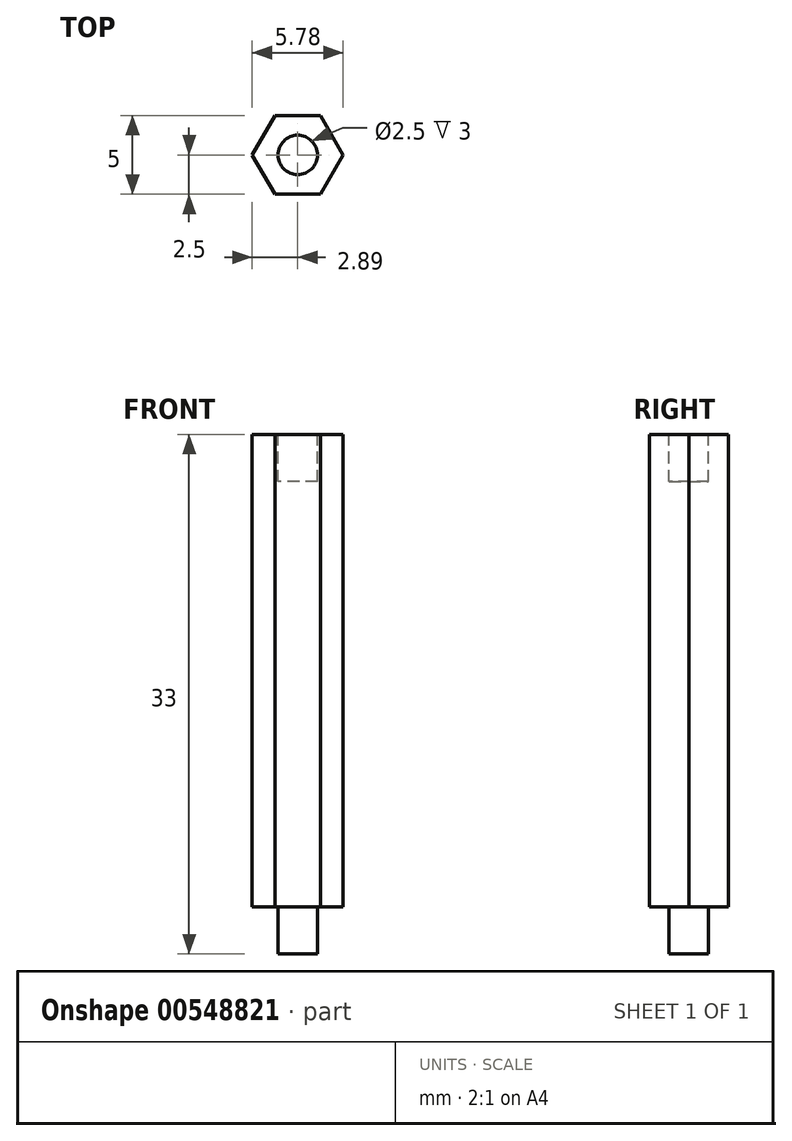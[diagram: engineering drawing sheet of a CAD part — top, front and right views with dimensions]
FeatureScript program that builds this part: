
annotation { "Feature Type Name" : "Feature", "Feature Type Description" : "" }
export const myFeature = defineFeature(function(context is Context, id is Id, definition is map)
    precondition{}
    {
        {
            var Q0;
            Q0=qCreatedBy(makeId("Top.planeOp"),FACE);
            var sketch = newSketch(context, id + "F0", { "sketchPlane" : qUnion([Q0])});
            skCircle(sketch, "E0", {"center": v(0, 0) * mm, "radius": 1.25 * mm});
            skSolve(sketch);
        }
        {
            var Q0;
            Q0 = qSketchRegion(id + "F0", true);
            extrude(context, id + "F1", {"entities" : qUnion([Q0]), "endBound" : BoundingType.SYMMETRIC, "oppositeDirection" : true, "depth" : 3 * mm, "offsetDistance" : 25 * mm});
        }
        {
            var Q0;
            Q0=makeQuery(id+"F1.opExtrude","CAP_FACE",FACE,{"disambiguationData":[OSD([sQuery(id+"F0.wireOp",EDGE,"E0")])],"isStart":true});
            var sketch = newSketch(context, id + "F2", { "sketchPlane" : qUnion([Q0])});
            skCircle(sketch, "E1.cCircle", {"center": v(0, 0) * mm, "radius": 2.5 * mm, "construction": true});
            skLineSegment(sketch, "E1.0", {"start": v(1.44, -2.5) * mm, "end": v(-1.44, -2.5) * mm});
            skLineSegment(sketch, "E1.1", {"start": v(-1.44, -2.5) * mm, "end": v(-2.89, 0) * mm});
            skLineSegment(sketch, "E1.2", {"start": v(-2.89, 0) * mm, "end": v(-1.44, 2.5) * mm});
            skLineSegment(sketch, "E1.3", {"start": v(-1.44, 2.5) * mm, "end": v(1.44, 2.5) * mm});
            skLineSegment(sketch, "E1.4", {"start": v(1.44, 2.5) * mm, "end": v(2.89, 0) * mm});
            skLineSegment(sketch, "E1.5", {"start": v(2.89, 0) * mm, "end": v(1.44, -2.5) * mm});
            skPoint(sketch, "E1.0.midPoint", {"position": v(0, -2.5) * mm});
            skSolve(sketch);
        }
        {
            var Q0;
            Q0=makeQuery(id+"F2.imprint","IMPRINT",FACE,{"disambiguationData":[TD([[makeQuery(id+"F2.imprint","IMPRINT",EDGE,{"derivedFrom":sQuery(id+"F2.wireOp",EDGE,"E1.0")}),-1.0]])]});
            var Q1;
            Q1=makeQuery(id+"F2.imprint","IMPRINT",FACE,{"disambiguationData":[TD([[makeQuery(id+"F2.imprint","IMPRINT",EDGE,{"derivedFrom":makeQuery(id+"F1.opExtrude","CAP_EDGE",EDGE,{"disambiguationData":[OSD([sQuery(id+"F0.wireOp",EDGE,"E0")])],"isStart":true})}),1.0]])]});
            extrude(context, id + "F3", {"entities" : qUnion([Q0, Q1]), "operationType" : NewBodyOperationType.ADD, "depth" : 30 * mm, "offsetDistance" : 25 * mm});
        }
        {
            var Q0;
            Q0=makeQuery(id+"F3.opExtrude","CAP_FACE",FACE,{"disambiguationData":[OSD([sQuery(id+"F2.wireOp",EDGE,"E1.0"),sQuery(id+"F2.wireOp",EDGE,"E1.1"),sQuery(id+"F2.wireOp",EDGE,"E1.2"),sQuery(id+"F2.wireOp",EDGE,"E1.3"),sQuery(id+"F2.wireOp",EDGE,"E1.4"),sQuery(id+"F2.wireOp",EDGE,"E1.5")])],"isStart":false});
            var sketch = newSketch(context, id + "F4", { "sketchPlane" : qUnion([Q0])});
            skCircle(sketch, "E2", {"center": v(0, 0) * mm, "radius": 1.25 * mm});
            skSolve(sketch);
        }
        {
            var Q0;
            Q0=makeQuery(id+"F4.imprint","IMPRINT",FACE,{"disambiguationData":[TD([[makeQuery(id+"F4.imprint","IMPRINT",EDGE,{"derivedFrom":sQuery(id+"F4.wireOp",EDGE,"E2")}),1.0]])]});
            extrude(context, id + "F5", {"entities" : qUnion([Q0]), "operationType" : NewBodyOperationType.REMOVE, "oppositeDirection" : true, "depth" : 3 * mm, "offsetDistance" : 25 * mm});
        }
    });
